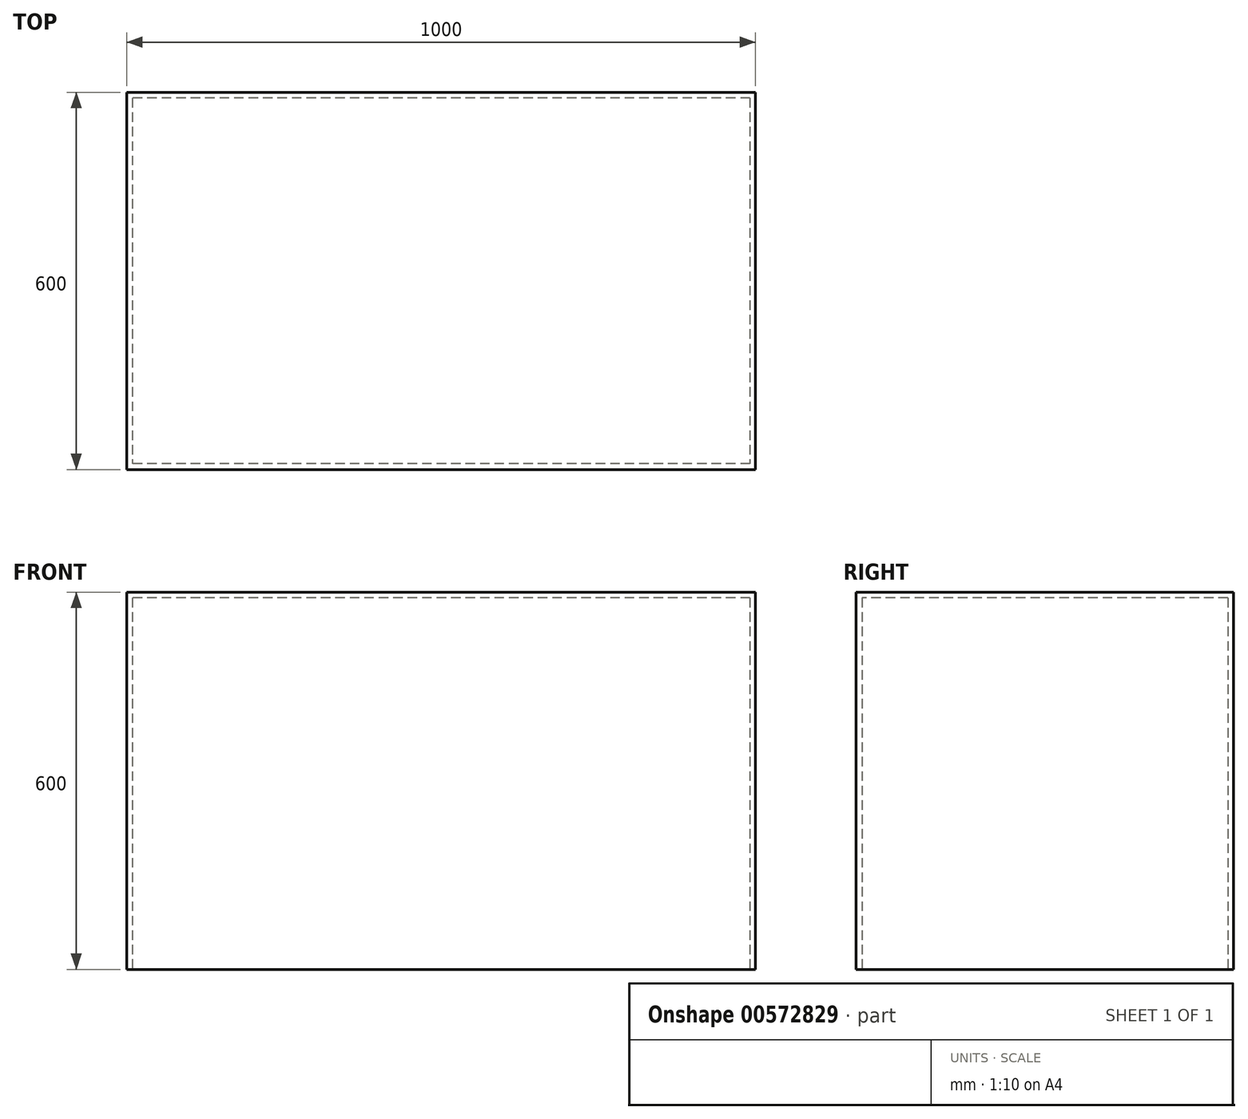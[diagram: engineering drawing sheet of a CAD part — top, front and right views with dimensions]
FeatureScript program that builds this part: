
annotation { "Feature Type Name" : "Feature", "Feature Type Description" : "" }
export const myFeature = defineFeature(function(context is Context, id is Id, definition is map)
    precondition{}
    {
        {
            var Q0;
            Q0=qCreatedBy(makeId("Top.planeOp"),FACE);
            var sketch = newSketch(context, id + "F0", { "sketchPlane" : qUnion([Q0])});
            skLineSegment(sketch, "E0.bottom", {"start": v(500, 300) * mm, "end": v(-500, 300) * mm});
            skLineSegment(sketch, "E0.top", {"start": v(500, -300) * mm, "end": v(-500, -300) * mm});
            skLineSegment(sketch, "E0.left", {"start": v(500, 300) * mm, "end": v(500, -300) * mm});
            skLineSegment(sketch, "E0.right", {"start": v(-500, 300) * mm, "end": v(-500, -300) * mm});
            skPoint(sketch, "E0.middle", {"position": v(0, 0) * mm});
            skSolve(sketch);
        }
        {
            var Q0;
            Q0=makeQuery(id+"F0.imprint","IMPRINT",FACE,{"disambiguationData":[TD([[makeQuery(id+"F0.imprint","IMPRINT",EDGE,{"derivedFrom":sQuery(id+"F0.wireOp",EDGE,"E0.bottom")}),1.0]])]});
            extrude(context, id + "F1", {"entities" : qUnion([Q0]), "depth" : 600 * mm, "offsetDistance" : 25 * mm});
        }
        {
            var Q0;
            Q0=makeQuery(id+"F1.opExtrude","CAP_FACE",FACE,{"disambiguationData":[OSD([sQuery(id+"F0.wireOp",EDGE,"E0.bottom"),sQuery(id+"F0.wireOp",EDGE,"E0.top"),sQuery(id+"F0.wireOp",EDGE,"E0.left"),sQuery(id+"F0.wireOp",EDGE,"E0.right")])],"isStart":true});
            shell(context, id + "F2", {"entities" : qUnion([Q0]), "thickness" : 9 * mm});
        }
    });
